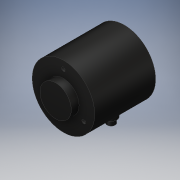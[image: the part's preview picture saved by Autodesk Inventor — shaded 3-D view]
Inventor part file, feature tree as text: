
AUTODESK INVENTOR PART (.ipt)
format: ipt  version: 2018 (Build 220112000, 112)  size: 155,648 bytes
history: native  units: mm
features: sketch x5, extrude x4, hole x1, plane x1, projected_geometry x1
ambient origin geometry x8: Origin, YZ Plane, XZ Plane, XY Plane, X Axis, Y Axis, Z Axis, Center Point
bodies: Solid1 (feature_tree)
feature tree (12):
  extrude  "Extrusion1"  Depth=39.0mm TaperAngle=0.0deg
  extrude  "Extrusion2"  Depth=20.0mm TaperAngle=0.0deg
  hole  "Hole1"  [1 undecoded]
  plane  "Work Plane2"
  extrude  "Extrusion6"  Depth=7.3mm
  extrude  "Extrusion7"  Depth=10.0mm
  sketch  "Sketch1"  dims[d0=40.0mm d1=39.0mm d2=0.0mm]
  sketch  "Sketch2"  dims[d3=20.0mm d4=5.0mm d5=0.0mm]
  sketch  "Sketch3"  dims[d6=30.0mm d7=30.0mm d9=360.0deg]
  sketch  "Sketch6"  dims[d11=2.459mm d12=7.0mm d13=4.0mm d14=2.0mm d15=90.0deg d16=9.8mm d17=20.594885mm d25=7.3mm]
  projected_geometry  "Projected Loop2"
  sketch  "Sketch7"  dims[d26=8.47mm d29=0.9mm d30=6.58mm d31=0.0mm d32=5.1mm d33=10.0mm d34=0.0mm d35=3.29mm d36=0.0mm]
note: 1 required parameter value undecoded (feature->parameter linkage not recoverable at this tier; creation-order binding heuristic only, values carry confidence <= 0.55)
